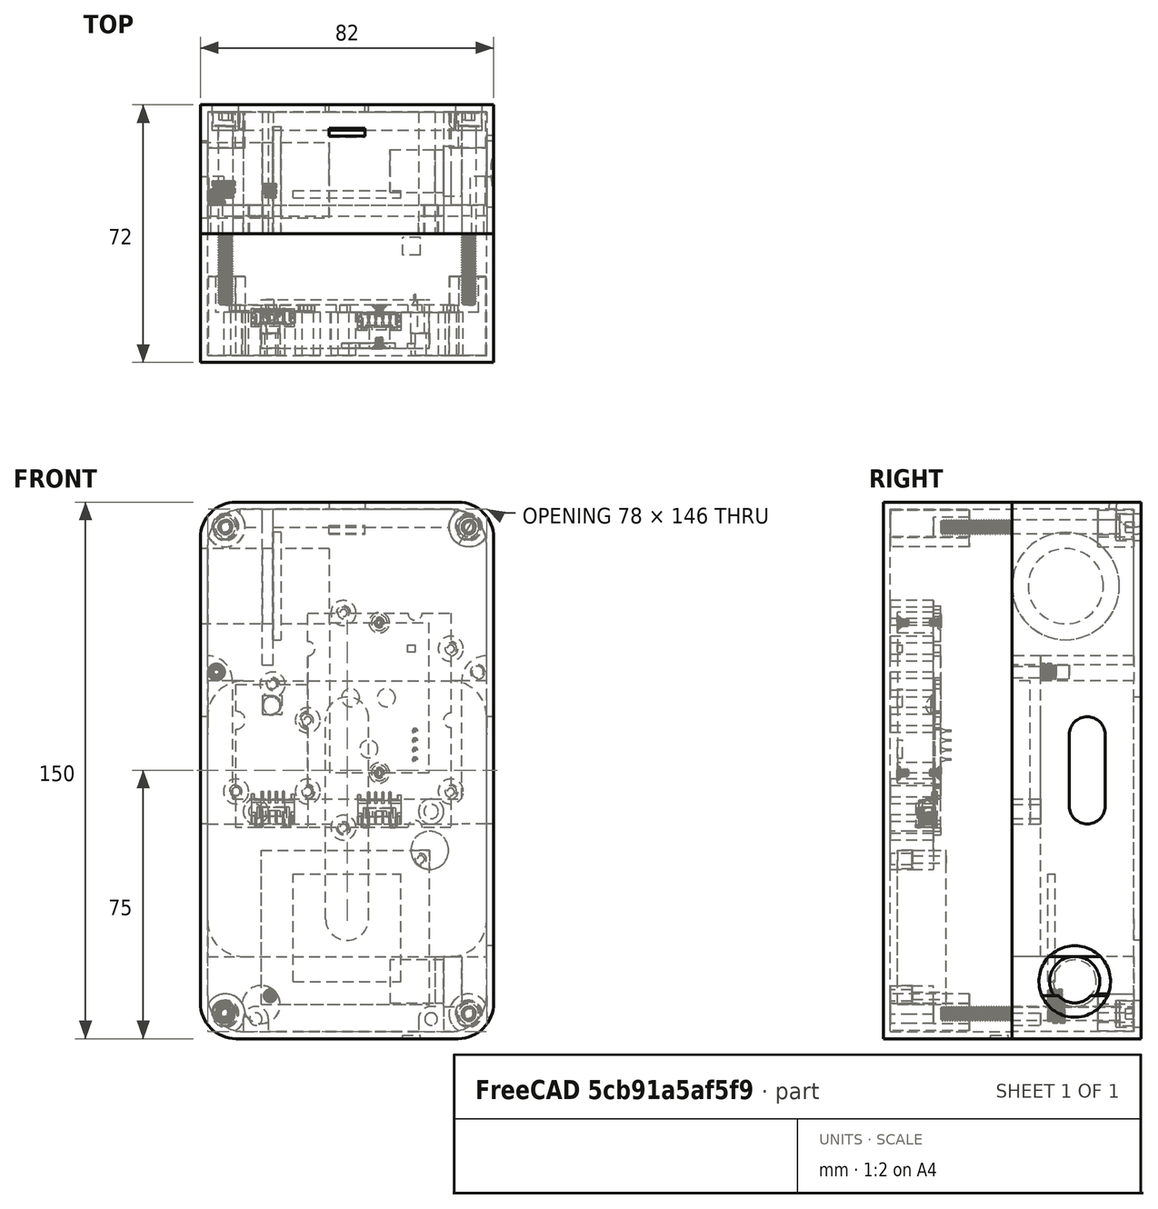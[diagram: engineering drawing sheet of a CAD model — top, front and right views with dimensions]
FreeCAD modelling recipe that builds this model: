
FCSTD DOCUMENT  (FreeCAD 0.20R29177 +233 (Git))
Label: wearableCad_10_11_2022
License: All rights reserved
LicenseURL: http://en.wikipedia.org/wiki/All_rights_reserved
objects: Part::Cylinder×103, Part::Cut×52, Part::Box×43, Part::MultiFuse×36, Part::Feature×10, Part::FeaturePython×1
note: 245 computed .brp shape members not serialized (recipe doc carries the construction recipe); baked Part::Feature solids carry a one-line shape summary decoded from their .brp

FEATURE [Part::Feature] Feature  label="Odroid-C4"
  Placement = pos=(66,-10,0) rot=(0.57735,-0.57735,0.57735;2.0944rad)
  shape: bbox 57.1 x 20.65 x 89.5 mm, 2775 faces, 0 solids (baked)
FEATURE [Part::Feature] Feature001  label="SCD30"
  Placement = pos=(-1.3e-14,-22,57) rot=(0,-1,0;1.5708rad)
  shape: bbox 44 x 15.1 x 64 mm, 422 faces, 13 solids (baked)
FEATURE [Part::Feature] Feature002  label="bme280"
  Placement = pos=(-60,-20,58) rot=(0.707107,0,0.707107;3.14159rad)
  shape: bbox 23.8 x 6.016 x 41.9 mm, 221 faces, 2 solids (baked)
FEATURE [Part::MultiFuse] Fusion  label="i2cSensors"
  Placement = pos=(68,-10,0) rot=(0,0,1;0rad)
  Shapes = -> [Feature001,Feature002]
FEATURE [Part::Box] Box  label="ips7100"
  AttacherType = Attacher::AttachEngine3D
  Height = 43.1
  Length = 47.1
  Width = 13.55
FEATURE [Part::Cylinder] Cylinder
  Angle = 360
  AttacherType = Attacher::AttachEngine3D
  FirstAngle = 0
  Height = 13.55
  Placement = pos=(2.5,13.55,2.5) rot=(1,0,0;1.5708rad)
  Radius = 1
  SecondAngle = 0
FEATURE [Part::Cylinder] Cylinder001  label="semiCut"
  Angle = 90
  AttacherType = Attacher::AttachEngine3D
  FirstAngle = 0
  Height = 4.13
  Placement = pos=(0,4.13,-9e-16) rot=(1,0,0;1.5708rad)
  Radius = 5.25
  SecondAngle = 0
FEATURE [Part::MultiFuse] Fusion001  label="ipsCut"
  Shapes = -> [Cylinder,Cylinder001]
FEATURE [Part::Cylinder] Cylinder002
  Angle = 360
  AttacherType = Attacher::AttachEngine3D
  FirstAngle = 0
  Height = 13.55
  Placement = pos=(2.5,13.55,2.5) rot=(1,0,0;1.5708rad)
  Radius = 1
  SecondAngle = 0
FEATURE [Part::Cylinder] Cylinder003  label="semiCut001"
  Angle = 90
  AttacherType = Attacher::AttachEngine3D
  FirstAngle = 0
  Height = 4.13
  Placement = pos=(0,4.13,-9e-16) rot=(1,0,0;1.5708rad)
  Radius = 5.25
  SecondAngle = 0
FEATURE [Part::MultiFuse] Fusion002  label="ipsCut001"
  Placement = pos=(47.1,0,43.1) rot=(0,1,0;3.14159rad)
  Shapes = -> [Cylinder002,Cylinder003]
FEATURE [Part::MultiFuse] Fusion003
  Shapes = -> [Fusion001,Fusion002]
FEATURE [Part::Cut] Cut  label="ips7100V"
  Base = -> Box
  Placement = pos=(15,-42,7.55) rot=(0,0,1;0rad)
  Tool = -> Fusion003
FEATURE [Part::Box] Box001  label="V25B"
  AttacherType = Attacher::AttachEngine3D
  Height = 77
  Length = 78
  Width = 26
FEATURE [Part::Cylinder] Cylinder004
  Angle = 90
  AttacherType = Attacher::AttachEngine3D
  FirstAngle = 0
  Height = 26
  Placement = pos=(0,26,-5.8e-15) rot=(1,0,0;1.5708rad)
  Radius = 10
  SecondAngle = 0
FEATURE [Part::Box] Box002  label="Cube"
  AttacherType = Attacher::AttachEngine3D
  Height = 10
  Length = 10
  Width = 26
FEATURE [Part::Cut] Cut001
  Base = -> Box002
  Placement = pos=(68,0,67) rot=(0,0,1;0rad)
  Tool = -> Cylinder004
FEATURE [Part::Box] Box003  label="Cube001"
  AttacherType = Attacher::AttachEngine3D
  Height = 10
  Length = 10
  Width = 26
FEATURE [Part::Cylinder] Cylinder005
  Angle = 90
  AttacherType = Attacher::AttachEngine3D
  FirstAngle = 0
  Height = 26
  Placement = pos=(0,26,-5.8e-15) rot=(1,0,0;1.5708rad)
  Radius = 10
  SecondAngle = 0
FEATURE [Part::Cut] Cut002
  Base = -> Box003
  Placement = pos=(68,0,10) rot=(0,1,0;1.5708rad)
  Tool = -> Cylinder005
FEATURE [Part::Box] Box004  label="Cube002"
  AttacherType = Attacher::AttachEngine3D
  Height = 10
  Length = 10
  Width = 26
FEATURE [Part::Cylinder] Cylinder006
  Angle = 90
  AttacherType = Attacher::AttachEngine3D
  FirstAngle = 0
  Height = 26
  Placement = pos=(0,26,-5.8e-15) rot=(1,0,0;1.5708rad)
  Radius = 10
  SecondAngle = 0
FEATURE [Part::Cut] Cut003
  Base = -> Box004
  Placement = pos=(10,0,10) rot=(0,1,0;3.14159rad)
  Tool = -> Cylinder006
FEATURE [Part::Box] Box005  label="Cube003"
  AttacherType = Attacher::AttachEngine3D
  Height = 10
  Length = 10
  Width = 26
FEATURE [Part::Cylinder] Cylinder007
  Angle = 90
  AttacherType = Attacher::AttachEngine3D
  FirstAngle = 0
  Height = 26
  Placement = pos=(0,26,-5.8e-15) rot=(1,0,0;1.5708rad)
  Radius = 10
  SecondAngle = 0
FEATURE [Part::Cut] Cut004
  Base = -> Box005
  Placement = pos=(10,0,67) rot=(0,-1,0;1.5708rad)
  Tool = -> Cylinder007
FEATURE [Part::MultiFuse] Fusion004  label="v25Cuts"
  Shapes = -> [Cut001,Cut002,Cut003,Cut004]
FEATURE [Part::Cut] Cut005  label="V25B001"
  Base = -> Box001
  Placement = pos=(0,-2,21) rot=(0,0,1;0rad)
  Tool = -> Fusion004
FEATURE [Part::Box] Box007  label="Cube004"
  AttacherType = Attacher::AttachEngine3D
  Height = 10
  Length = 10
  Placement = pos=(0,-10,0) rot=(0,0,1;0rad)
  Width = 36
FEATURE [Part::Cylinder] Cylinder008
  Angle = 90
  AttacherType = Attacher::AttachEngine3D
  FirstAngle = 0
  Height = 36
  Placement = pos=(0,26,-5.8e-15) rot=(1,0,0;1.5708rad)
  Radius = 10
  SecondAngle = 0
FEATURE [Part::Cut] Cut006
  Base = -> Box007
  Placement = pos=(8,18,8) rot=(0.707107,0,-0.707107;3.14159rad)
  Tool = -> Cylinder008
FEATURE [Part::Box] Box008  label="baseOut001"
  AttacherType = Attacher::AttachEngine3D
  Height = 150
  Length = 82
  Placement = pos=(80,26,-2) rot=(0,0,1;3.14159rad)
  Width = 36
FEATURE [Part::Box] Box009  label="Cube005"
  AttacherType = Attacher::AttachEngine3D
  Height = 10
  Length = 10
  Placement = pos=(0,-10,0) rot=(0,0,1;0rad)
  Width = 36
FEATURE [Part::Cylinder] Cylinder009
  Angle = 90
  AttacherType = Attacher::AttachEngine3D
  FirstAngle = 0
  Height = 36
  Placement = pos=(0,26,-5.8e-15) rot=(1,0,0;1.5708rad)
  Radius = 10
  SecondAngle = 0
FEATURE [Part::Cut] Cut007
  Base = -> Box009
  Placement = pos=(70,18,8) rot=(1,0,0;3.14159rad)
  Tool = -> Cylinder009
FEATURE [Part::Box] Box010  label="Cube006"
  AttacherType = Attacher::AttachEngine3D
  Height = 10
  Length = 10
  Placement = pos=(0,-10,0) rot=(0,0,1;0rad)
  Width = 36
FEATURE [Part::Cylinder] Cylinder010
  Angle = 90
  AttacherType = Attacher::AttachEngine3D
  FirstAngle = 0
  Height = 36
  Placement = pos=(0,26,-5.8e-15) rot=(1,0,0;1.5708rad)
  Radius = 10
  SecondAngle = 0
FEATURE [Part::Cut] Cut008
  Base = -> Box010
  Placement = pos=(8,18,138) rot=(0,0,1;3.14159rad)
  Tool = -> Cylinder010
FEATURE [Part::Box] Box011  label="Cube007"
  AttacherType = Attacher::AttachEngine3D
  Height = 10
  Length = 10
  Placement = pos=(0,-10,0) rot=(0,0,1;0rad)
  Width = 36
FEATURE [Part::Cylinder] Cylinder011
  Angle = 90
  AttacherType = Attacher::AttachEngine3D
  FirstAngle = 0
  Height = 36
  Placement = pos=(0,26,-5.8e-15) rot=(1,0,0;1.5708rad)
  Radius = 10
  SecondAngle = 0
FEATURE [Part::Cut] Cut009
  Base = -> Box011
  Placement = pos=(70,18,138) rot=(0.707107,0,0.707107;3.14159rad)
  Tool = -> Cylinder011
FEATURE [Part::MultiFuse] Fusion005
  Placement = pos=(0,-2,0) rot=(0,0,1;0rad)
  Shapes = -> [Cut006,Cut007,Cut008,Cut009]
FEATURE [Part::Cut] Cut010  label="BaseOut"
  Base = -> Box008
  Tool = -> Fusion005
FEATURE [Part::Box] Box013  label="Cube009"
  AttacherType = Attacher::AttachEngine3D
  Height = 10
  Length = 10
  Placement = pos=(0,-8,0) rot=(0,0,1;0rad)
  Width = 34
FEATURE [Part::Box] Box014  label="baseOut002"
  AttacherType = Attacher::AttachEngine3D
  Height = 146
  Length = 78
  Placement = pos=(80,26,-2) rot=(0,0,1;3.14159rad)
  Width = 34
FEATURE [Part::Box] Box015  label="Cube010"
  AttacherType = Attacher::AttachEngine3D
  Height = 10
  Length = 10
  Placement = pos=(0,-8,0) rot=(0,0,1;0rad)
  Width = 34
FEATURE [Part::Box] Box016  label="Cube011"
  AttacherType = Attacher::AttachEngine3D
  Height = 10
  Length = 10
  Placement = pos=(0,-8,0) rot=(0,0,1;0rad)
  Width = 34
FEATURE [Part::Box] Box017  label="Cube012"
  AttacherType = Attacher::AttachEngine3D
  Height = 10
  Length = 10
  Placement = pos=(0,-8,0) rot=(0,0,1;0rad)
  Width = 34
FEATURE [Part::Cylinder] Cylinder013
  Angle = 90
  AttacherType = Attacher::AttachEngine3D
  FirstAngle = 0
  Height = 34
  Placement = pos=(0,26,-5.8e-15) rot=(1,0,0;1.5708rad)
  Radius = 10
  SecondAngle = 0
FEATURE [Part::Cut] Cut012
  Base = -> Box013
  Placement = pos=(12,18,8) rot=(0.707107,0,-0.707107;3.14159rad)
  Tool = -> Cylinder013
FEATURE [Part::Cylinder] Cylinder014
  Angle = 90
  AttacherType = Attacher::AttachEngine3D
  FirstAngle = 0
  Height = 34
  Placement = pos=(0,26,-5.8e-15) rot=(1,0,0;1.5708rad)
  Radius = 10
  SecondAngle = 0
FEATURE [Part::Cut] Cut013
  Base = -> Box015
  Placement = pos=(70,18,8) rot=(1,0,0;3.14159rad)
  Tool = -> Cylinder014
FEATURE [Part::Cylinder] Cylinder015
  Angle = 90
  AttacherType = Attacher::AttachEngine3D
  FirstAngle = 0
  Height = 34
  Placement = pos=(0,26,-5.8e-15) rot=(1,0,0;1.5708rad)
  Radius = 10
  SecondAngle = 0
FEATURE [Part::Cut] Cut014
  Base = -> Box016
  Placement = pos=(12,18,134) rot=(0,0,1;3.14159rad)
  Tool = -> Cylinder015
FEATURE [Part::Cylinder] Cylinder016
  Angle = 90
  AttacherType = Attacher::AttachEngine3D
  FirstAngle = 0
  Height = 34
  Placement = pos=(0,26,-5.8e-15) rot=(1,0,0;1.5708rad)
  Radius = 10
  SecondAngle = 0
FEATURE [Part::Cut] Cut015
  Base = -> Box017
  Placement = pos=(70,18,134) rot=(0.707107,0,0.707107;3.14159rad)
  Tool = -> Cylinder016
FEATURE [Part::MultiFuse] Fusion006
  Shapes = -> [Cut012,Cut013,Cut014,Cut015]
FEATURE [Part::Cut] Cut016  label="BaseOut001"
  Base = -> Box014
  Placement = pos=(-2,-2,2) rot=(0,0,1;0rad)
  Tool = -> Fusion006
FEATURE [Part::Cut] Cut017  label="baseOut"
  Base = -> Cut010
  Tool = -> Cut016
FEATURE [Part::Box] Box018  label="Cube013"
  AttacherType = Attacher::AttachEngine3D
  Height = 10
  Length = 10
  Placement = pos=(10,26,0) rot=(0,0,1;3.14159rad)
  Width = 26
FEATURE [Part::Cylinder] Cylinder017
  Angle = 90
  AttacherType = Attacher::AttachEngine3D
  FirstAngle = 0
  Height = 26
  Placement = pos=(0,26,-5.8e-15) rot=(1,0,0;1.5708rad)
  Radius = 10
  SecondAngle = 0
FEATURE [Part::Cut] Cut018  label="batterySupport"
  Base = -> Box018
  Placement = pos=(10,-2,31) rot=(0,1,0;3.14159rad)
  Tool = -> Cylinder017
FEATURE [Part::Box] Box019  label="Cube014"
  AttacherType = Attacher::AttachEngine3D
  Height = 10
  Length = 10
  Placement = pos=(10,26,0) rot=(0,0,1;3.14159rad)
  Width = 26
FEATURE [Part::Cylinder] Cylinder018
  Angle = 90
  AttacherType = Attacher::AttachEngine3D
  FirstAngle = 0
  Height = 26
  Placement = pos=(0,26,-5.8e-15) rot=(1,0,0;1.5708rad)
  Radius = 10
  SecondAngle = 0
FEATURE [Part::Cut] Cut019  label="batterySupport001"
  Base = -> Box019
  Placement = pos=(68,-2,31) rot=(0,1,0;1.5708rad)
  Tool = -> Cylinder018
FEATURE [Part::Box] Box020  label="Cube015"
  AttacherType = Attacher::AttachEngine3D
  Height = 10
  Length = 10
  Placement = pos=(10,26,0) rot=(0,0,1;3.14159rad)
  Width = 26
FEATURE [Part::Cylinder] Cylinder019
  Angle = 90
  AttacherType = Attacher::AttachEngine3D
  FirstAngle = 0
  Height = 26
  Placement = pos=(0,26,-5.8e-15) rot=(1,0,0;1.5708rad)
  Radius = 10
  SecondAngle = 0
FEATURE [Part::Cut] Cut020  label="batterySupport002"
  Base = -> Box020
  Placement = pos=(68,-2,88) rot=(0,0,1;0rad)
  Tool = -> Cylinder019
FEATURE [Part::Box] Box021  label="Cube016"
  AttacherType = Attacher::AttachEngine3D
  Height = 10
  Length = 10
  Placement = pos=(10,26,0) rot=(0,0,1;3.14159rad)
  Width = 26
FEATURE [Part::Cylinder] Cylinder020
  Angle = 90
  AttacherType = Attacher::AttachEngine3D
  FirstAngle = 0
  Height = 26
  Placement = pos=(0,26,-5.8e-15) rot=(1,0,0;1.5708rad)
  Radius = 10
  SecondAngle = 0
FEATURE [Part::Cut] Cut021  label="batterySupport003"
  Base = -> Box021
  Placement = pos=(10,-2,88) rot=(0,-1,0;1.5708rad)
  Tool = -> Cylinder020
FEATURE [Part::Cylinder] Cylinder021
  Angle = 360
  AttacherType = Attacher::AttachEngine3D
  FirstAngle = 0
  Height = 34
  Placement = pos=(13.5,24,3.5) rot=(1,0,0;1.5708rad)
  Radius = 3.5
  SecondAngle = 0
FEATURE [Part::Cylinder] Cylinder022
  Angle = 360
  AttacherType = Attacher::AttachEngine3D
  FirstAngle = 0
  Height = 8
  Placement = pos=(13.5,-2,3.5) rot=(1,0,0;1.5708rad)
  Radius = 1.75
  SecondAngle = 0
FEATURE [Part::Box] Box022  label="Cube017"
  AttacherType = Attacher::AttachEngine3D
  Height = 3.5
  Length = 7
  Placement = pos=(10,24,3.5) rot=(1,0,0;3.14159rad)
  Width = 34
FEATURE [Part::Cylinder] Cylinder023
  Angle = 360
  AttacherType = Attacher::AttachEngine3D
  FirstAngle = 0
  Height = 34
  Placement = pos=(62.5,24,3.5) rot=(1,0,0;1.5708rad)
  Radius = 3.5
  SecondAngle = 0
FEATURE [Part::Cylinder] Cylinder024
  Angle = 360
  AttacherType = Attacher::AttachEngine3D
  FirstAngle = 0
  Height = 8
  Placement = pos=(62.5,-2,3.5) rot=(1,0,0;1.5708rad)
  Radius = 1.75
  SecondAngle = 0
FEATURE [Part::Box] Box023  label="Cube018"
  AttacherType = Attacher::AttachEngine3D
  Height = 3.5
  Length = 7
  Placement = pos=(59,24,3.5) rot=(1,0,0;3.14159rad)
  Width = 34
FEATURE [Part::Cylinder] Cylinder025
  Angle = 360
  AttacherType = Attacher::AttachEngine3D
  FirstAngle = 0
  Height = 20
  Radius = 6
  SecondAngle = 0
FEATURE [Part::Cylinder] Cylinder026
  Angle = 360
  AttacherType = Attacher::AttachEngine3D
  FirstAngle = 0
  Height = 5
  Radius = 7
  SecondAngle = 0
FEATURE [Part::MultiFuse] Fusion007  label="powerSwitch"
  Placement = pos=(71,7.5,14) rot=(0,-1,0;1.5708rad)
  Shapes = -> [Cylinder025,Cylinder026]
FEATURE [Part::Box] Box024  label="Cube019"
  AttacherType = Attacher::AttachEngine3D
  Height = 17.5
  Length = 2.5
  Placement = pos=(63.5,24,21) rot=(1,0,0;3.14159rad)
  Width = 34
FEATURE [Part::MultiFuse] Fusion008  label="base"
  Shapes = -> [Cut017,Cut018,Cut019,Cut020,Cut021]
FEATURE [Part::MultiFuse] Fusion009  label="base001"
  Shapes = -> [Cylinder021,Cylinder023,Box022,Box023,Box024,Fusion008]
FEATURE [Part::MultiFuse] Fusion010  label="baseCuts"
  Shapes = -> [Cylinder024,Cylinder022,Fusion007]
FEATURE [Part::Cut] Cut022  label="base002"
  Base = -> Fusion009
  Tool = -> Fusion010
FEATURE [Part::Cylinder] Cylinder027  label="mainMounts"
  Angle = 90
  AttacherType = Attacher::AttachEngine3D
  FirstAngle = 0
  Height = 26
  Placement = pos=(0,24,98) rot=(1,0,0;1.5708rad)
  Radius = 7
  SecondAngle = 0
FEATURE [Part::Cylinder] Cylinder028  label="mainMounts001"
  Angle = 90
  AttacherType = Attacher::AttachEngine3D
  FirstAngle = 0
  Height = 26
  Placement = pos=(78,24,98) rot=(0.57735,-0.57735,0.57735;2.0944rad)
  Radius = 7
  SecondAngle = 0
FEATURE [Part::Cylinder] Cylinder029
  Angle = 360
  AttacherType = Attacher::AttachEngine3D
  FirstAngle = 0
  Height = 8
  Placement = pos=(2.5,-2,100.5) rot=(1,0,0;1.5708rad)
  Radius = 2
  SecondAngle = 0
FEATURE [Part::Cylinder] Cylinder030
  Angle = 360
  AttacherType = Attacher::AttachEngine3D
  FirstAngle = 0
  Height = 8
  Placement = pos=(75.5,-2,100.5) rot=(1,0,0;1.5708rad)
  Radius = 2
  SecondAngle = 0
FEATURE [Part::MultiFuse] Fusion011  label="baseCuts001"
  Placement = pos=(0,8,0) rot=(0,0,1;0rad)
  Shapes = -> [Cylinder029,Cylinder030]
FEATURE [Part::MultiFuse] Fusion012
  Shapes = -> [Cylinder028,Cylinder027]
FEATURE [Part::MultiFuse] Fusion013  label="base003"
  Shapes = -> [Cut022,Fusion012]
FEATURE [Part::Cut] Cut023  label="baseBottom"
  Base = -> Fusion013
  Tool = -> Fusion011
FEATURE [Part::Feature] Solid  label="m3HeatSet"
  Placement = pos=(2.5,2.3,100.5) rot=(1,0,0;3.14159rad)
  shape: bbox 4.772 x 4.354 x 4.772 mm, 239 faces (baked)
FEATURE [Part::Cylinder] Cylinder031
  Angle = 360
  AttacherType = Attacher::AttachEngine3D
  FirstAngle = 0
  Height = 8
  Placement = pos=(13.5,-2,61.5) rot=(1,0,0;1.5708rad)
  Radius = 3.5
  SecondAngle = 0
FEATURE [Part::Cylinder] Cylinder032  label="cuts"
  Angle = 360
  AttacherType = Attacher::AttachEngine3D
  FirstAngle = 0
  Height = 8
  Placement = pos=(13.5,-2,61.5) rot=(1,0,0;1.5708rad)
  Radius = 2
  SecondAngle = 0
FEATURE [Part::Cylinder] Cylinder034
  Angle = 360
  AttacherType = Attacher::AttachEngine3D
  FirstAngle = 0
  Height = 8
  Placement = pos=(62.5,-2,61.5) rot=(1,0,0;1.5708rad)
  Radius = 3.5
  SecondAngle = 0
FEATURE [Part::Cylinder] Cylinder035  label="cuts001"
  Angle = 360
  AttacherType = Attacher::AttachEngine3D
  FirstAngle = 0
  Height = 8
  Placement = pos=(62.5,-2,61.5) rot=(1,0,0;1.5708rad)
  Radius = 2
  SecondAngle = 0
FEATURE [Part::Cylinder] Cylinder036
  Angle = 90
  AttacherType = Attacher::AttachEngine3D
  FirstAngle = 0
  Height = 8
  Placement = pos=(78,-2,98) rot=(0.57735,-0.57735,0.57735;2.0944rad)
  Radius = 7
  SecondAngle = 0
FEATURE [Part::Cylinder] Cylinder037
  Angle = 90
  AttacherType = Attacher::AttachEngine3D
  FirstAngle = 0
  Height = 8
  Placement = pos=(0,-2,98) rot=(1,0,0;1.5708rad)
  Radius = 7
  SecondAngle = 0
FEATURE [Part::Box] Box025  label="Cube020"
  AttacherType = Attacher::AttachEngine3D
  Height = 7
  Length = 78
  Placement = pos=(0,-5,58) rot=(0,0,1;0rad)
  Width = 3
FEATURE [Part::Box] Box026  label="Cube021"
  AttacherType = Attacher::AttachEngine3D
  Height = 7
  Length = 40
  Placement = pos=(7,-5,58) rot=(0,-1,0;1.5708rad)
  Width = 3
FEATURE [Part::Box] Box027  label="Cube022"
  AttacherType = Attacher::AttachEngine3D
  Height = 7
  Length = 40
  Placement = pos=(78,-5,58) rot=(0,-1,0;1.5708rad)
  Width = 3
FEATURE [Part::MultiFuse] Fusion014
  Shapes = -> [Box027,Box025,Box026,Cylinder034,Cylinder031]
FEATURE [Part::Cylinder] Cylinder038  label="m3Screw"
  Angle = 360
  AttacherType = Attacher::AttachEngine3D
  FirstAngle = 0
  Height = 8
  Placement = pos=(75.5,-2,100.5) rot=(1,0,0;1.5708rad)
  Radius = 1.6
  SecondAngle = 0
FEATURE [Part::Cylinder] Cylinder039  label="m3Screw001"
  Angle = 360
  AttacherType = Attacher::AttachEngine3D
  FirstAngle = 0
  Height = 8
  Placement = pos=(2.5,-2,100.5) rot=(1,0,0;1.5708rad)
  Radius = 1.6
  SecondAngle = 0
FEATURE [Part::MultiFuse] Fusion015  label="c4Hold"
  Shapes = -> [Cylinder036,Cylinder037,Fusion014]
FEATURE [Part::MultiFuse] Fusion016  label="c4oldCuts"
  Shapes = -> [Cylinder039,Cylinder032,Cylinder035,Cylinder038]
FEATURE [Part::Cut] Cut024  label="c4Hold001"
  Base = -> Fusion015
  Tool = -> Fusion016
FEATURE [Part::Box] Box028  label="Cube023"
  AttacherType = Attacher::AttachEngine3D
  Height = 10
  Length = 10
  Placement = pos=(0,-10,0) rot=(0,0,1;0rad)
  Width = 36
FEATURE [Part::Box] Box029  label="baseOut003"
  AttacherType = Attacher::AttachEngine3D
  Height = 150
  Length = 82
  Placement = pos=(80,26,-2) rot=(0,0,1;3.14159rad)
  Width = 36
FEATURE [Part::Box] Box030  label="Cube024"
  AttacherType = Attacher::AttachEngine3D
  Height = 10
  Length = 10
  Placement = pos=(0,-10,0) rot=(0,0,1;0rad)
  Width = 36
FEATURE [Part::Box] Box031  label="Cube025"
  AttacherType = Attacher::AttachEngine3D
  Height = 10
  Length = 10
  Placement = pos=(0,-10,0) rot=(0,0,1;0rad)
  Width = 36
FEATURE [Part::Box] Box032  label="Cube026"
  AttacherType = Attacher::AttachEngine3D
  Height = 10
  Length = 10
  Placement = pos=(0,-10,0) rot=(0,0,1;0rad)
  Width = 36
FEATURE [Part::Box] Box033  label="Cube027"
  AttacherType = Attacher::AttachEngine3D
  Height = 10
  Length = 10
  Placement = pos=(0,-8,0) rot=(0,0,1;0rad)
  Width = 34
FEATURE [Part::Box] Box034  label="baseOut004"
  AttacherType = Attacher::AttachEngine3D
  Height = 146
  Length = 78
  Placement = pos=(80,26,-2) rot=(0,0,1;3.14159rad)
  Width = 34
FEATURE [Part::Box] Box035  label="Cube028"
  AttacherType = Attacher::AttachEngine3D
  Height = 10
  Length = 10
  Placement = pos=(0,-8,0) rot=(0,0,1;0rad)
  Width = 34
FEATURE [Part::Box] Box036  label="Cube029"
  AttacherType = Attacher::AttachEngine3D
  Height = 10
  Length = 10
  Placement = pos=(0,-8,0) rot=(0,0,1;0rad)
  Width = 34
FEATURE [Part::Box] Box037  label="Cube030"
  AttacherType = Attacher::AttachEngine3D
  Height = 10
  Length = 10
  Placement = pos=(0,-8,0) rot=(0,0,1;0rad)
  Width = 34
FEATURE [Part::Cylinder] Cylinder040
  Angle = 90
  AttacherType = Attacher::AttachEngine3D
  FirstAngle = 0
  Height = 36
  Placement = pos=(0,26,-5.8e-15) rot=(1,0,0;1.5708rad)
  Radius = 10
  SecondAngle = 0
FEATURE [Part::Cut] Cut025
  Base = -> Box028
  Placement = pos=(8,18,8) rot=(0.707107,0,-0.707107;3.14159rad)
  Tool = -> Cylinder040
FEATURE [Part::Cylinder] Cylinder041
  Angle = 90
  AttacherType = Attacher::AttachEngine3D
  FirstAngle = 0
  Height = 36
  Placement = pos=(0,26,-5.8e-15) rot=(1,0,0;1.5708rad)
  Radius = 10
  SecondAngle = 0
FEATURE [Part::Cut] Cut026
  Base = -> Box030
  Placement = pos=(70,18,8) rot=(1,0,0;3.14159rad)
  Tool = -> Cylinder041
FEATURE [Part::Cylinder] Cylinder042
  Angle = 90
  AttacherType = Attacher::AttachEngine3D
  FirstAngle = 0
  Height = 36
  Placement = pos=(0,26,-5.8e-15) rot=(1,0,0;1.5708rad)
  Radius = 10
  SecondAngle = 0
FEATURE [Part::Cut] Cut027
  Base = -> Box031
  Placement = pos=(8,18,138) rot=(0,0,1;3.14159rad)
  Tool = -> Cylinder042
FEATURE [Part::Cylinder] Cylinder043
  Angle = 90
  AttacherType = Attacher::AttachEngine3D
  FirstAngle = 0
  Height = 36
  Placement = pos=(0,26,-5.8e-15) rot=(1,0,0;1.5708rad)
  Radius = 10
  SecondAngle = 0
FEATURE [Part::Cut] Cut028
  Base = -> Box032
  Placement = pos=(70,18,138) rot=(0.707107,0,0.707107;3.14159rad)
  Tool = -> Cylinder043
FEATURE [Part::Cylinder] Cylinder044
  Angle = 90
  AttacherType = Attacher::AttachEngine3D
  FirstAngle = 0
  Height = 34
  Placement = pos=(0,26,-5.8e-15) rot=(1,0,0;1.5708rad)
  Radius = 10
  SecondAngle = 0
FEATURE [Part::Cut] Cut030
  Base = -> Box033
  Placement = pos=(12,18,8) rot=(0.707107,0,-0.707107;3.14159rad)
  Tool = -> Cylinder044
FEATURE [Part::Cylinder] Cylinder045
  Angle = 90
  AttacherType = Attacher::AttachEngine3D
  FirstAngle = 0
  Height = 34
  Placement = pos=(0,26,-5.8e-15) rot=(1,0,0;1.5708rad)
  Radius = 10
  SecondAngle = 0
FEATURE [Part::Cut] Cut031
  Base = -> Box035
  Placement = pos=(70,18,8) rot=(1,0,0;3.14159rad)
  Tool = -> Cylinder045
FEATURE [Part::Cylinder] Cylinder046
  Angle = 90
  AttacherType = Attacher::AttachEngine3D
  FirstAngle = 0
  Height = 34
  Placement = pos=(0,26,-5.8e-15) rot=(1,0,0;1.5708rad)
  Radius = 10
  SecondAngle = 0
FEATURE [Part::Cut] Cut032
  Base = -> Box036
  Placement = pos=(12,18,134) rot=(0,0,1;3.14159rad)
  Tool = -> Cylinder046
FEATURE [Part::Cylinder] Cylinder047
  Angle = 90
  AttacherType = Attacher::AttachEngine3D
  FirstAngle = 0
  Height = 34
  Placement = pos=(0,26,-5.8e-15) rot=(1,0,0;1.5708rad)
  Radius = 10
  SecondAngle = 0
FEATURE [Part::Cut] Cut033
  Base = -> Box037
  Placement = pos=(70,18,134) rot=(0.707107,0,0.707107;3.14159rad)
  Tool = -> Cylinder047
FEATURE [Part::MultiFuse] Fusion017
  Placement = pos=(0,-2,0) rot=(0,0,1;0rad)
  Shapes = -> [Cut025,Cut026,Cut027,Cut028]
FEATURE [Part::Cut] Cut029  label="BaseOut002"
  Base = -> Box029
  Tool = -> Fusion017
FEATURE [Part::MultiFuse] Fusion018
  Shapes = -> [Cut030,Cut031,Cut032,Cut033]
FEATURE [Part::Cut] Cut034  label="BaseOut003"
  Base = -> Box034
  Placement = pos=(-2,-2,2) rot=(0,0,1;0rad)
  Tool = -> Fusion018
FEATURE [Part::Cut] Cut035  label="baseTop"
  Base = -> Cut029
  Placement = pos=(78,-20,0) rot=(0,0,1;3.14159rad)
  Tool = -> Cut034
FEATURE [Part::Feature] Solid001  label="m2HeatSet"
  Placement = pos=(17.5,0,10) rot=(0,0,1;0rad)
  shape: bbox 3.655 x 4.083 x 3.655 mm, 239 faces (baked)
FEATURE [Part::Cylinder] Cylinder048
  Angle = 360
  AttacherType = Attacher::AttachEngine3D
  FirstAngle = 0
  Height = 6
  Placement = pos=(17.5,-44,10.05) rot=(-1,0,0;1.5708rad)
  Radius = 1.57
  SecondAngle = 0
FEATURE [Part::Cylinder] Cylinder049
  Angle = 360
  AttacherType = Attacher::AttachEngine3D
  FirstAngle = 0
  Height = 6
  Placement = pos=(15,-44,7.55) rot=(0.57735,0.57735,0.57735;4.18879rad)
  Radius = 5.3
  SecondAngle = 0
FEATURE [Part::Cylinder] Cylinder050
  Angle = 360
  AttacherType = Attacher::AttachEngine3D
  FirstAngle = 0
  Height = 6
  Placement = pos=(62.1,-44,50.65) rot=(0.57735,-0.57735,-0.57735;4.18879rad)
  Radius = 5.3
  SecondAngle = 0
FEATURE [Part::Cylinder] Cylinder051
  Angle = 360
  AttacherType = Attacher::AttachEngine3D
  FirstAngle = 0
  Height = 6
  Placement = pos=(59.6,-44,48.15) rot=(-1,0,0;1.5708rad)
  Radius = 1.57
  SecondAngle = 0
FEATURE [Part::Cut] Cut036
  Base = -> Cylinder049
  Tool = -> Cylinder048
FEATURE [Part::Cut] Cut037
  Base = -> Cylinder050
  Tool = -> Cylinder051
FEATURE [Part::Cylinder] Cylinder052
  Angle = 270
  AttacherType = Attacher::AttachEngine3D
  FirstAngle = 0
  Height = 6
  Placement = pos=(15,-38,7.55) rot=(-1,0,0;1.5708rad)
  Radius = 5.3
  SecondAngle = 0
FEATURE [Part::Cylinder] Cylinder053
  Angle = 270
  AttacherType = Attacher::AttachEngine3D
  FirstAngle = 0
  Height = 6
  Placement = pos=(62.1,-38,50.65) rot=(0,0.707107,0.707107;3.14159rad)
  Radius = 5.3
  SecondAngle = 0
FEATURE [Part::MultiFuse] Fusion019  label="baseTop001"
  Shapes = -> [Cut036,Cut037,Cylinder052,Cylinder053,Cut035]
FEATURE [Part::Cylinder] Cylinder054  label="m2HeatSet001"
  Angle = 360
  AttacherType = Attacher::AttachEngine3D
  FirstAngle = 0
  Height = 12
  Placement = pos=(8,-44,67.1) rot=(-1,0,0;1.5708rad)
  Radius = 1.6
  SecondAngle = 0
FEATURE [Part::Cylinder] Cylinder055  label="m2HeatSet002"
  Angle = 360
  AttacherType = Attacher::AttachEngine3D
  FirstAngle = 0
  Height = 12
  Placement = pos=(28,-44,67.1) rot=(-1,0,0;1.5708rad)
  Radius = 1.6
  SecondAngle = 0
FEATURE [Part::Cylinder] Cylinder056  label="m2HeatSet003"
  Angle = 360
  AttacherType = Attacher::AttachEngine3D
  FirstAngle = 0
  Height = 12
  Placement = pos=(68,-44,67.1) rot=(-1,0,0;1.5708rad)
  Radius = 1.6
  SecondAngle = 0
FEATURE [Part::Cylinder] Cylinder057  label="m2HeatSet004"
  Angle = 360
  AttacherType = Attacher::AttachEngine3D
  FirstAngle = 0
  Height = 12
  Placement = pos=(18.2,-44,97) rot=(-1,0,0;1.5708rad)
  Radius = 1.6
  SecondAngle = 0
FEATURE [Part::Cylinder] Cylinder058  label="m2HeatSet005"
  Angle = 360
  AttacherType = Attacher::AttachEngine3D
  FirstAngle = 0
  Height = 12
  Placement = pos=(28,-44,87) rot=(-1,0,0;1.5708rad)
  Radius = 1.6
  SecondAngle = 0
FEATURE [Part::Cylinder] Cylinder059  label="m2HeatSet006"
  Angle = 360
  AttacherType = Attacher::AttachEngine3D
  FirstAngle = 0
  Height = 12
  Placement = pos=(38,-44,117) rot=(-1,0,0;1.5708rad)
  Radius = 1.6
  SecondAngle = 0
FEATURE [Part::Cylinder] Cylinder060  label="m2HeatSet007"
  Angle = 360
  AttacherType = Attacher::AttachEngine3D
  FirstAngle = 0
  Height = 12
  Placement = pos=(38,-44,57) rot=(-1,0,0;1.5708rad)
  Radius = 1.6
  SecondAngle = 0
FEATURE [Part::Cylinder] Cylinder061  label="m2HeatSet008"
  Angle = 360
  AttacherType = Attacher::AttachEngine3D
  FirstAngle = 0
  Height = 12
  Placement = pos=(68,-44,107) rot=(-1,0,0;1.5708rad)
  Radius = 1.6
  SecondAngle = 0
FEATURE [Part::Cylinder] Cylinder062  label="m2HeatSetOut"
  Angle = 360
  AttacherType = Attacher::AttachEngine3D
  FirstAngle = 0
  Height = 12
  Placement = pos=(8,-44,67.1) rot=(-1,0,0;1.5708rad)
  Radius = 3.5
  SecondAngle = 0
FEATURE [Part::Cylinder] Cylinder063  label="m2HeatSetOut001"
  Angle = 360
  AttacherType = Attacher::AttachEngine3D
  FirstAngle = 0
  Height = 12
  Placement = pos=(28,-44,67.1) rot=(-1,0,0;1.5708rad)
  Radius = 3.5
  SecondAngle = 0
FEATURE [Part::Cylinder] Cylinder064  label="m2HeatSetOut002"
  Angle = 360
  AttacherType = Attacher::AttachEngine3D
  FirstAngle = 0
  Height = 12
  Placement = pos=(18.2,-44,97) rot=(-1,0,0;1.5708rad)
  Radius = 3.5
  SecondAngle = 0
FEATURE [Part::Cylinder] Cylinder065  label="m2HeatSetOut003"
  Angle = 360
  AttacherType = Attacher::AttachEngine3D
  FirstAngle = 0
  Height = 12
  Placement = pos=(68,-44,67.1) rot=(-1,0,0;1.5708rad)
  Radius = 3.5
  SecondAngle = 0
FEATURE [Part::Cylinder] Cylinder066  label="m2HeatSetOut004"
  Angle = 360
  AttacherType = Attacher::AttachEngine3D
  FirstAngle = 0
  Height = 12
  Placement = pos=(28,-44,87) rot=(-1,0,0;1.5708rad)
  Radius = 3.5
  SecondAngle = 0
FEATURE [Part::Cylinder] Cylinder067  label="m2HeatSetOut005"
  Angle = 360
  AttacherType = Attacher::AttachEngine3D
  FirstAngle = 0
  Height = 12
  Placement = pos=(38,-44,57) rot=(-1,0,0;1.5708rad)
  Radius = 3.5
  SecondAngle = 0
FEATURE [Part::Cylinder] Cylinder068  label="m2HeatSetOut006"
  Angle = 360
  AttacherType = Attacher::AttachEngine3D
  FirstAngle = 0
  Height = 12
  Placement = pos=(68,-44,107) rot=(-1,0,0;1.5708rad)
  Radius = 3.5
  SecondAngle = 0
FEATURE [Part::Cylinder] Cylinder069  label="m2HeatSetOut007"
  Angle = 360
  AttacherType = Attacher::AttachEngine3D
  FirstAngle = 0
  Height = 12
  Placement = pos=(38,-44,117) rot=(-1,0,0;1.5708rad)
  Radius = 3.5
  SecondAngle = 0
FEATURE [Part::MultiFuse] Fusion020  label="baseTop002"
  Shapes = -> [Cylinder069,Cylinder063,Cylinder064,Cylinder065,Cylinder066,Cylinder067,Cylinder068,Fusion019]
FEATURE [Part::MultiFuse] Fusion021  label="m2HeatSetCuts"
  Shapes = -> [Cylinder062,Cylinder054,Cylinder055,Cylinder056,Cylinder057,Cylinder058,Cylinder059,Cylinder060,Cylinder061]
FEATURE [Part::Cut] Cut038  label="baseTop003"
  Base = -> Fusion020
  Tool = -> Fusion021
FEATURE [Part::Cylinder] Cylinder070
  Angle = 360
  AttacherType = Attacher::AttachEngine3D
  FirstAngle = 0
  Height = 20
  Radius = 6
  SecondAngle = 0
FEATURE [Part::Cylinder] Cylinder071
  Angle = 360
  AttacherType = Attacher::AttachEngine3D
  FirstAngle = 0
  Height = 5
  Radius = 7
  SecondAngle = 0
FEATURE [Part::MultiFuse] Fusion022  label="powerSwitch001"
  Placement = pos=(71,7.5,14) rot=(0,-1,0;1.5708rad)
  Shapes = -> [Cylinder070,Cylinder071]
FEATURE [Part::Feature] Solid002  label="M4Screw"
  Placement = pos=(73,-30,5) rot=(0.57735,-0.57735,0.57735;2.0944rad)
  shape: bbox 7.001 x 54.15 x 7.001 mm, 147 faces (baked)
FEATURE [Part::Feature] Solid003  label="M4Screw001"
  Placement = pos=(5,-30,5) rot=(0.57735,-0.57735,0.57735;2.0944rad)
  shape: bbox 7.001 x 54.15 x 7.001 mm, 147 faces (baked)
FEATURE [Part::Feature] Solid004  label="M4Screw002"
  Placement = pos=(5,-30,141) rot=(0.57735,-0.57735,0.57735;2.0944rad)
  shape: bbox 7.001 x 54.15 x 7.001 mm, 147 faces (baked)
FEATURE [Part::Feature] Solid005  label="M4Screw003"
  Placement = pos=(73,-30,141) rot=(0.57735,-0.57735,0.57735;2.0944rad)
  shape: bbox 7.001 x 54.15 x 7.001 mm, 147 faces (baked)
FEATURE [Part::Cylinder] Cylinder072  label="m4HoleBase"
  Angle = 360
  AttacherType = Attacher::AttachEngine3D
  FirstAngle = 0
  Height = 22
  Placement = pos=(4.5,-44,141.5) rot=(0.377964,0.654654,0.654654;3.86433rad)
  Radius = 5.5
  SecondAngle = 0
FEATURE [Part::Cylinder] Cylinder073  label="m4HeatSetCut"
  Angle = 360
  AttacherType = Attacher::AttachEngine3D
  FirstAngle = 0
  Height = 10
  Placement = pos=(4.5,-32,141.5) rot=(-1,0,0;1.5708rad)
  Radius = 2.8
  SecondAngle = 0
FEATURE [Part::Cut] Cut039  label="m4HeatSetHoles"
  Base = -> Cylinder072
  Placement = pos=(0.5,0,-0.5) rot=(0,0,1;0rad)
  Tool = -> Cylinder073
FEATURE [Part::Cylinder] Cylinder074  label="m4HoleBase001"
  Angle = 360
  AttacherType = Attacher::AttachEngine3D
  FirstAngle = 0
  Height = 22
  Placement = pos=(4.5,-44,141.5) rot=(0.38203,0.653473,0.653473;3.86433rad)
  Radius = 5.5
  SecondAngle = 0
FEATURE [Part::Cylinder] Cylinder075  label="m4HeatSetCut001"
  Angle = 360
  AttacherType = Attacher::AttachEngine3D
  FirstAngle = 0
  Height = 10
  Placement = pos=(4.5,-32,141.5) rot=(-1,0,0;1.5708rad)
  Radius = 2.8
  SecondAngle = 0
FEATURE [Part::Cut] Cut040  label="m4HeatSetHoles001"
  Base = -> Cylinder074
  Placement = pos=(68.5,0,-0.5) rot=(0,0,1;0rad)
  Tool = -> Cylinder075
FEATURE [Part::Cylinder] Cylinder076  label="m4HoleBase002"
  Angle = 360
  AttacherType = Attacher::AttachEngine3D
  FirstAngle = 0
  Height = 22
  Placement = pos=(4.5,-44,141.5) rot=(0.377964,0.654654,0.654654;3.86433rad)
  Radius = 5.5
  SecondAngle = 0
FEATURE [Part::Cylinder] Cylinder077  label="m4HeatSetCut002"
  Angle = 360
  AttacherType = Attacher::AttachEngine3D
  FirstAngle = 0
  Height = 10
  Placement = pos=(4.5,-32,141.5) rot=(-1,0,0;1.5708rad)
  Radius = 2.8
  SecondAngle = 0
FEATURE [Part::Cut] Cut041  label="m4HeatSetHoles002"
  Base = -> Cylinder076
  Placement = pos=(0.5,0,-136.5) rot=(0,0,1;0rad)
  Tool = -> Cylinder077
FEATURE [Part::Cylinder] Cylinder078  label="m4HoleBase003"
  Angle = 360
  AttacherType = Attacher::AttachEngine3D
  FirstAngle = 0
  Height = 22
  Placement = pos=(4.5,-44,141.5) rot=(0.377964,0.654654,0.654654;3.86433rad)
  Radius = 5.5
  SecondAngle = 0
FEATURE [Part::Cylinder] Cylinder079  label="m4HeatSetCut003"
  Angle = 360
  AttacherType = Attacher::AttachEngine3D
  FirstAngle = 0
  Height = 10
  Placement = pos=(4.5,-32,141.5) rot=(-1,0,0;1.5708rad)
  Radius = 2.8
  SecondAngle = 0
FEATURE [Part::Cut] Cut042  label="m4HeatSetHoles003"
  Base = -> Cylinder078
  Placement = pos=(68.5,0,-136.5) rot=(0,0,1;0rad)
  Tool = -> Cylinder079
FEATURE [Part::MultiFuse] Fusion023  label="baseTop004"
  Shapes = -> [Cut039,Cut040,Cut041,Cut042,Cut038]
FEATURE [Part::Feature] Solid006  label="m4HeatSet"
  Placement = pos=(4.5,0,5.5) rot=(0,0,1;0rad)
  shape: bbox 6.396 x 4.801 x 6.396 mm, 237 faces (baked)
FEATURE [Part::Cylinder] Cylinder080  label="m2HeatSetOut008"
  Angle = 360
  AttacherType = Attacher::AttachEngine3D
  FirstAngle = 0
  Height = 12
  Placement = pos=(8,-44,67.1) rot=(-1,0,0;1.5708rad)
  Radius = 3.5
  SecondAngle = 0
FEATURE [Part::Cylinder] Cylinder081  label="m2HeatSet009"
  Angle = 360
  AttacherType = Attacher::AttachEngine3D
  FirstAngle = 0
  Height = 12
  Placement = pos=(8,-44,67.1) rot=(-1,0,0;1.5708rad)
  Radius = 1.6
  SecondAngle = 0
FEATURE [Part::Cut] Cut043  label="m2HeatSet010"
  Base = -> Cylinder080
  Tool = -> Cylinder081
FEATURE [Part::MultiFuse] Fusion024  label="baseTop005"
  Shapes = -> [Fusion023,Cut043]
FEATURE [Part::Cylinder] Cylinder084  label="m4HoleBase006"
  Angle = 360
  AttacherType = Attacher::AttachEngine3D
  FirstAngle = 0
  Height = 12
  Placement = pos=(73,26,5) rot=(0,-0.707107,0.707107;3.14159rad)
  Radius = 5.5
  SecondAngle = 0
FEATURE [Part::Cylinder] Cylinder085  label="m4HoleBaseCut"
  Angle = 360
  AttacherType = Attacher::AttachEngine3D
  FirstAngle = 0
  Height = 7
  Placement = pos=(73,26,5) rot=(0,0.707107,-0.707107;3.14159rad)
  Radius = 3.75
  SecondAngle = 0
FEATURE [Part::Cylinder] Cylinder086  label="m4HoleBase007"
  Angle = 360
  AttacherType = Attacher::AttachEngine3D
  FirstAngle = 0
  Height = 12
  Placement = pos=(5,26,5) rot=(0,-0.707107,0.707107;3.14159rad)
  Radius = 5.5
  SecondAngle = 0
FEATURE [Part::Cylinder] Cylinder087  label="m4HoleBaseCut001"
  Angle = 360
  AttacherType = Attacher::AttachEngine3D
  FirstAngle = 0
  Height = 7
  Placement = pos=(5,26,5) rot=(0,-0.707107,0.707107;3.14159rad)
  Radius = 3.75
  SecondAngle = 0
FEATURE [Part::Cylinder] Cylinder088  label="m4HoleBase008"
  Angle = 360
  AttacherType = Attacher::AttachEngine3D
  FirstAngle = 0
  Height = 12
  Placement = pos=(73,26,141) rot=(0,-0.707107,0.707107;3.14159rad)
  Radius = 5.5
  SecondAngle = 0
FEATURE [Part::Cylinder] Cylinder089  label="m4HoleBaseCut002"
  Angle = 360
  AttacherType = Attacher::AttachEngine3D
  FirstAngle = 0
  Height = 7
  Placement = pos=(73,26,141) rot=(0,-0.707107,0.707107;3.14159rad)
  Radius = 3.75
  SecondAngle = 0
FEATURE [Part::Cylinder] Cylinder090  label="m4HoleBase009"
  Angle = 360
  AttacherType = Attacher::AttachEngine3D
  FirstAngle = 0
  Height = 12
  Placement = pos=(5,26,141) rot=(0,-0.707107,0.707107;3.14159rad)
  Radius = 5.5
  SecondAngle = 0
FEATURE [Part::Cylinder] Cylinder091  label="m4HoleBaseCut003"
  Angle = 360
  AttacherType = Attacher::AttachEngine3D
  FirstAngle = 0
  Height = 7
  Placement = pos=(5,26,141) rot=(0,-0.707107,0.707107;3.14159rad)
  Radius = 3.75
  SecondAngle = 0
FEATURE [Part::MultiFuse] Fusion025  label="baseBottom001"
  Shapes = -> [Cylinder084,Cylinder086,Cylinder088,Cylinder090,Cut023]
FEATURE [Part::MultiFuse] Fusion026  label="m4Cuts"
  Shapes = -> [Cylinder085,Cylinder087,Cylinder089,Cylinder091]
FEATURE [Part::Cut] Cut044  label="baseBottom002"
  Base = -> Fusion025
  Tool = -> Fusion026
FEATURE [Part::Cylinder] Cylinder092  label="m4HoleBaseCut004"
  Angle = 360
  AttacherType = Attacher::AttachEngine3D
  FirstAngle = 0
  Height = 7
  Placement = pos=(73,26,5) rot=(0,0.707107,-0.707107;3.14159rad)
  Radius = 2.1
  SecondAngle = 0
FEATURE [Part::Cylinder] Cylinder093  label="m4HoleBaseCut005"
  Angle = 360
  AttacherType = Attacher::AttachEngine3D
  FirstAngle = 0
  Height = 7
  Placement = pos=(5,26,5) rot=(0,0.707107,-0.707107;3.14159rad)
  Radius = 2.1
  SecondAngle = 0
FEATURE [Part::Cylinder] Cylinder094  label="m4HoleBaseCut006"
  Angle = 360
  AttacherType = Attacher::AttachEngine3D
  FirstAngle = 0
  Height = 7
  Placement = pos=(73,26,141) rot=(0,0.707107,-0.707107;3.14159rad)
  Radius = 2.1
  SecondAngle = 0
FEATURE [Part::Cylinder] Cylinder095  label="m4HoleBaseCut007"
  Angle = 360
  AttacherType = Attacher::AttachEngine3D
  FirstAngle = 0
  Height = 7
  Placement = pos=(5,26,141) rot=(0,0.707107,-0.707107;3.14159rad)
  Radius = 2.1
  SecondAngle = 0
FEATURE [Part::MultiFuse] Fusion027  label="m4Cuts001"
  Placement = pos=(0,-5,0) rot=(0,0,1;0rad)
  Shapes = -> [Cylinder092,Cylinder093,Cylinder094,Cylinder095]
FEATURE [Part::Cut] Cut045  label="baseBottom003"
  Base = -> Cut044
  Tool = -> Fusion027
FEATURE [Part::Cylinder] Cylinder096
  Angle = 360
  AttacherType = Attacher::AttachEngine3D
  FirstAngle = 0
  Height = 20
  Radius = 6
  SecondAngle = 0
FEATURE [Part::Cylinder] Cylinder097
  Angle = 360
  AttacherType = Attacher::AttachEngine3D
  FirstAngle = 0
  Height = 5
  Radius = 10
  SecondAngle = 0
FEATURE [Part::MultiFuse] Fusion028  label="Switch"
  Placement = pos=(83,7.5,14) rot=(0,-1,0;1.5708rad)
  Shapes = -> [Cylinder096,Cylinder097]
FEATURE [Part::Cylinder] Cylinder098  label="Ethernet"
  Angle = 360
  AttacherType = Attacher::AttachEngine3D
  FirstAngle = 0
  Height = 36
  Radius = 10.5
  SecondAngle = 0
FEATURE [Part::Cylinder] Cylinder099  label="Ethernet001"
  Angle = 360
  AttacherType = Attacher::AttachEngine3D
  FirstAngle = 0
  Height = 2.25
  Placement = pos=(0,0,13.5) rot=(0,0,1;0rad)
  Radius = 15
  SecondAngle = 0
FEATURE [Part::MultiFuse] Fusion029  label="EthenetCut"
  Placement = pos=(34,5,124.5) rot=(0,1,0;4.71239rad)
  Shapes = -> [Cylinder098,Cylinder099]
FEATURE [Part::Box] Box038  label="ethernetHold"
  AttacherType = Attacher::AttachEngine3D
  Height = 34
  Length = 3
  Placement = pos=(15.3,24,102.5) rot=(1,0,0;1.5708rad)
  Width = 43.5
FEATURE [Part::Cylinder] Cylinder100  label="Ethernet002"
  Angle = 360
  AttacherType = Attacher::AttachEngine3D
  FirstAngle = 0
  Height = 36
  Radius = 10.5
  SecondAngle = 0
FEATURE [Part::Cylinder] Cylinder101  label="Ethernet003"
  Angle = 360
  AttacherType = Attacher::AttachEngine3D
  FirstAngle = 0
  Height = 2.25
  Placement = pos=(0,0,13.5) rot=(0,0,1;0rad)
  Radius = 15
  SecondAngle = 0
FEATURE [Part::MultiFuse] Fusion030  label="Ethenet001"
  Placement = pos=(34,5,124.5) rot=(0,-1,0;1.5708rad)
  Shapes = -> [Cylinder100,Cylinder101]
FEATURE [Part::MultiFuse] Fusion031  label="baseBottom004"
  Shapes = -> [Cut045,Box038]
FEATURE [Part::Cylinder] Cylinder102  label="hookReinforment"
  Angle = 90
  AttacherType = Attacher::AttachEngine3D
  FirstAngle = 0
  Height = 60
  Placement = pos=(9,24,146) rot=(0.57735,-0.57735,0.57735;4.18879rad)
  Radius = 5
  SecondAngle = 0
FEATURE [Part::FeaturePython] Tube  label="hookCut"  # WARN: FeaturePython — macro-defined, semantics opaque (R4)
  AttacherType = Attacher::AttachEngine3D
  Height = 10
  InnerRadius = 5
  OuterRadius = 7
  Placement = pos=(34,24,146) rot=(0,1,0;1.5708rad)
FEATURE [Part::MultiFuse] Fusion032  label="baseBottom005"
  Shapes = -> [Fusion031,Cylinder102]
FEATURE [Part::MultiFuse] Fusion033  label="baseBottomCuts"
  Shapes = -> [Fusion029,Fusion028,Tube]
FEATURE [Part::Cut] Cut046  label="baseBottom006"
  Base = -> Fusion032
  Tool = -> Fusion033
FEATURE [Part::Box] Box039  label="usbCut"
  AttacherType = Attacher::AttachEngine3D
  Height = 10
  Length = 82
  Width = 30
FEATURE [Part::Cylinder] Cylinder103
  Angle = 180
  AttacherType = Attacher::AttachEngine3D
  FirstAngle = 0
  Height = 82
  Placement = pos=(0,5,5) rot=(0.707107,0,0.707107;3.14159rad)
  Radius = 5
  SecondAngle = 0
FEATURE [Part::Box] Box040  label="Cube032"
  AttacherType = Attacher::AttachEngine3D
  Height = 10
  Length = 82
  Width = 5
FEATURE [Part::Cut] Cut047  label="cornerCuts"
  Base = -> Box040
  Tool = -> Cylinder103
FEATURE [Part::Box] Box041  label="Cube033"
  AttacherType = Attacher::AttachEngine3D
  Height = 10
  Length = 82
  Width = 5
FEATURE [Part::Cylinder] Cylinder104
  Angle = 180
  AttacherType = Attacher::AttachEngine3D
  FirstAngle = 0
  Height = 82
  Placement = pos=(0,5,5) rot=(0.707107,0,0.707107;3.14159rad)
  Radius = 5
  SecondAngle = 0
FEATURE [Part::Cut] Cut048  label="cornerCuts001"
  Base = -> Box041
  Placement = pos=(0,30,10) rot=(1,0,0;3.14159rad)
  Tool = -> Cylinder104
FEATURE [Part::MultiFuse] Fusion034
  Shapes = -> [Cut047,Cut048]
FEATURE [Part::Cut] Cut049  label="usbCut001"
  Base = -> Box039
  Placement = pos=(-2,16,58) rot=(1,0,0;1.5708rad)
  Tool = -> Fusion034
FEATURE [Part::Cut] Cut050  label="baseBottom007"
  Base = -> Cut046
  Tool = -> Cut049
FEATURE [Part::Box] Box042  label="Cube034"
  AttacherType = Attacher::AttachEngine3D
  Height = 56
  Length = 12
  Width = 2
FEATURE [Part::Cylinder] Cylinder105
  Angle = 360
  AttacherType = Attacher::AttachEngine3D
  FirstAngle = 0
  Height = 2
  Placement = pos=(6,0,0) rot=(0,0.707107,0.707107;3.14159rad)
  Radius = 6
  SecondAngle = 0
FEATURE [Part::Cylinder] Cylinder106
  Angle = 360
  AttacherType = Attacher::AttachEngine3D
  FirstAngle = 0
  Height = 2
  Placement = pos=(6,1.24e-14,56) rot=(0,0.707107,0.707107;3.14159rad)
  Radius = 6
  SecondAngle = 0
FEATURE [Part::MultiFuse] Fusion035  label="voltaicCut"
  Placement = pos=(33,24,31.5) rot=(0,0,1;0rad)
  Shapes = -> [Cylinder106,Cylinder105,Box042]
FEATURE [Part::Cut] Cut051  label="baseBottom008"
  Base = -> Cut050
  Tool = -> Fusion035
FEATURE [Part::Box] Box043  label="lightCut"
  AttacherType = Attacher::AttachEngine3D
  Height = 5
  Length = 5
  Placement = pos=(54.5,-16,-6) rot=(0,0,1;0rad)
  Width = 5
FEATURE [Part::Cut] Cut052  label="baseTop006"
  Base = -> Fusion024
  Tool = -> Box043
FEATURE [Part::Box] Box044  label="Cube035"
  AttacherType = Attacher::AttachEngine3D
  Height = 30
  Length = 30
  Placement = pos=(24,0,14) rot=(0,0,1;0rad)
  Width = 2
